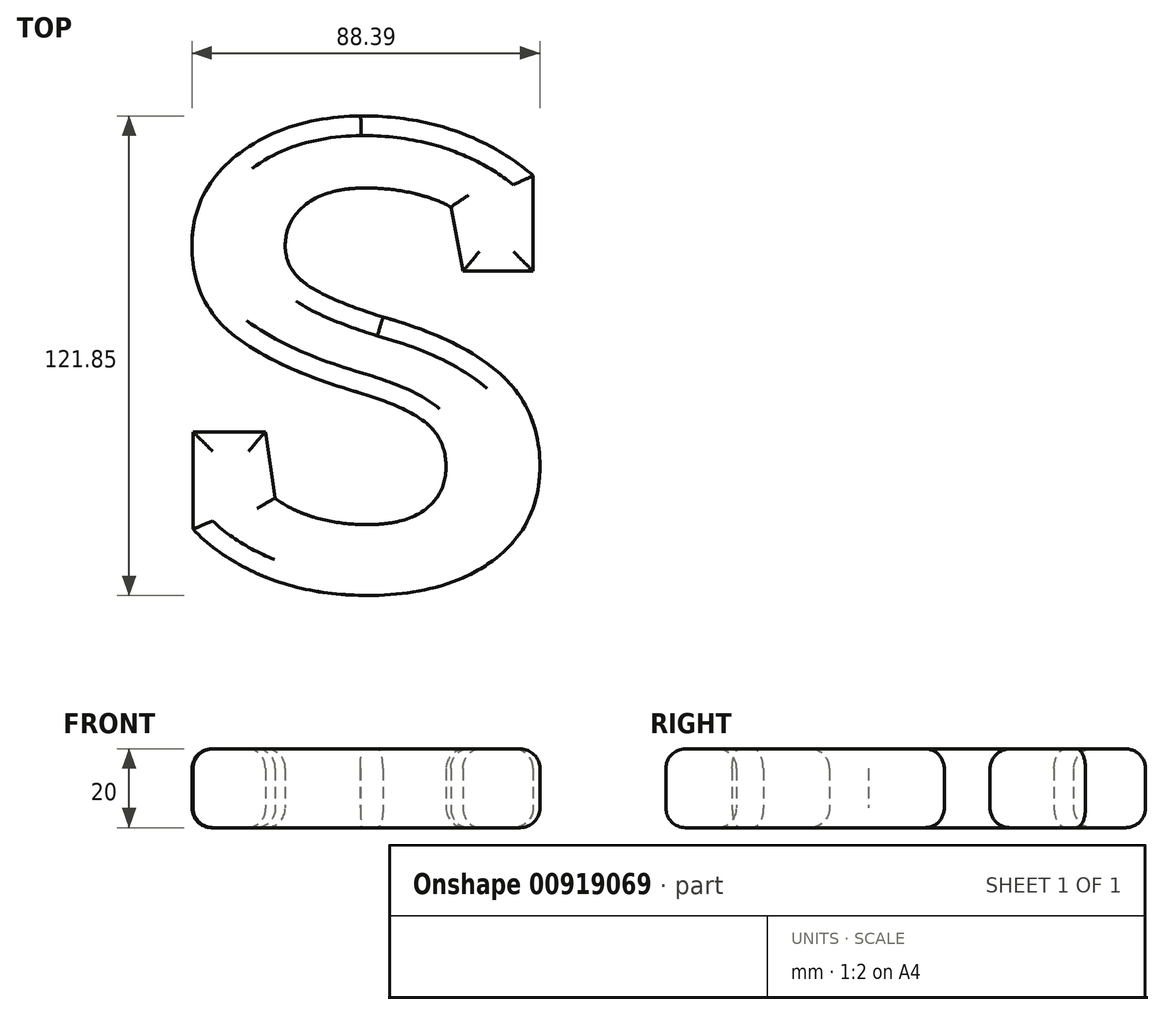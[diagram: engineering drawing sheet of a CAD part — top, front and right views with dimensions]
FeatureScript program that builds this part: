
annotation { "Feature Type Name" : "Feature", "Feature Type Description" : "" }
export const myFeature = defineFeature(function(context is Context, id is Id, definition is map)
    precondition{}
    {
        {
            var Q0;
            Q0=qCreatedBy(makeId("Top.planeOp"),FACE);
            var sketch = newSketch(context, id + "F0", { "sketchPlane" : qUnion([Q0])});
            skText(sketch, "E0", { "text": "S", "fontName": "RobotoSlab-Bold.ttf"});
            const initialGuessF0  = {"E0": [-0.07053, -0.06391, 1, 0, 0.12]};
            skSetInitialGuess(sketch, initialGuessF0);
            skSolve(sketch);
        }
        {
            var Q0;
            Q0 = qSketchRegion(id + "F0", true);
            extrude(context, id + "F1", {"entities" : qUnion([Q0]), "depth" : 20 * mm, "offsetDistance" : 25 * mm});
        }
        {
            var Q0;
            Q0=makeQuery(id+"F1.opExtrude","CAP_FACE",FACE,{"disambiguationData":[OSD([sQuery(id+"F0.wireOp",EDGE,"E0.sketch_text.stroke-0"),sQuery(id+"F0.wireOp",EDGE,"E0.sketch_text.stroke-1"),sQuery(id+"F0.wireOp",EDGE,"E0.sketch_text.stroke-2"),sQuery(id+"F0.wireOp",EDGE,"E0.sketch_text.stroke-3"),sQuery(id+"F0.wireOp",EDGE,"E0.sketch_text.stroke-4"),sQuery(id+"F0.wireOp",EDGE,"E0.sketch_text.stroke-5"),sQuery(id+"F0.wireOp",EDGE,"E0.sketch_text.stroke-6"),sQuery(id+"F0.wireOp",EDGE,"E0.sketch_text.stroke-7"),sQuery(id+"F0.wireOp",EDGE,"E0.sketch_text.stroke-8"),sQuery(id+"F0.wireOp",EDGE,"E0.sketch_text.stroke-9"),sQuery(id+"F0.wireOp",EDGE,"E0.sketch_text.stroke-10"),sQuery(id+"F0.wireOp",EDGE,"E0.sketch_text.stroke-11"),sQuery(id+"F0.wireOp",EDGE,"E0.sketch_text.stroke-12"),sQuery(id+"F0.wireOp",EDGE,"E0.sketch_text.stroke-13"),sQuery(id+"F0.wireOp",EDGE,"E0.sketch_text.stroke-14"),sQuery(id+"F0.wireOp",EDGE,"E0.sketch_text.stroke-15"),sQuery(id+"F0.wireOp",EDGE,"E0.sketch_text.stroke-16"),sQuery(id+"F0.wireOp",EDGE,"E0.sketch_text.stroke-17"),sQuery(id+"F0.wireOp",EDGE,"E0.sketch_text.stroke-18"),sQuery(id+"F0.wireOp",EDGE,"E0.sketch_text.stroke-19"),sQuery(id+"F0.wireOp",EDGE,"E0.sketch_text.stroke-20"),sQuery(id+"F0.wireOp",EDGE,"E0.sketch_text.stroke-21"),sQuery(id+"F0.wireOp",EDGE,"E0.sketch_text.stroke-22"),sQuery(id+"F0.wireOp",EDGE,"E0.sketch_text.stroke-23"),sQuery(id+"F0.wireOp",EDGE,"E0.sketch_text.stroke-24"),sQuery(id+"F0.wireOp",EDGE,"E0.sketch_text.stroke-25"),sQuery(id+"F0.wireOp",EDGE,"E0.sketch_text.stroke-26"),sQuery(id+"F0.wireOp",EDGE,"E0.sketch_text.stroke-27"),sQuery(id+"F0.wireOp",EDGE,"E0.sketch_text.stroke-28"),sQuery(id+"F0.wireOp",EDGE,"E0.sketch_text.stroke-29")])],"isStart":true});
            var Q1;
            Q1=makeQuery(id+"F1.opExtrude","CAP_FACE",FACE,{"disambiguationData":[OSD([sQuery(id+"F0.wireOp",EDGE,"E0.sketch_text.stroke-0"),sQuery(id+"F0.wireOp",EDGE,"E0.sketch_text.stroke-1"),sQuery(id+"F0.wireOp",EDGE,"E0.sketch_text.stroke-2"),sQuery(id+"F0.wireOp",EDGE,"E0.sketch_text.stroke-3"),sQuery(id+"F0.wireOp",EDGE,"E0.sketch_text.stroke-4"),sQuery(id+"F0.wireOp",EDGE,"E0.sketch_text.stroke-5"),sQuery(id+"F0.wireOp",EDGE,"E0.sketch_text.stroke-6"),sQuery(id+"F0.wireOp",EDGE,"E0.sketch_text.stroke-7"),sQuery(id+"F0.wireOp",EDGE,"E0.sketch_text.stroke-8"),sQuery(id+"F0.wireOp",EDGE,"E0.sketch_text.stroke-9"),sQuery(id+"F0.wireOp",EDGE,"E0.sketch_text.stroke-10"),sQuery(id+"F0.wireOp",EDGE,"E0.sketch_text.stroke-11"),sQuery(id+"F0.wireOp",EDGE,"E0.sketch_text.stroke-12"),sQuery(id+"F0.wireOp",EDGE,"E0.sketch_text.stroke-13"),sQuery(id+"F0.wireOp",EDGE,"E0.sketch_text.stroke-14"),sQuery(id+"F0.wireOp",EDGE,"E0.sketch_text.stroke-15"),sQuery(id+"F0.wireOp",EDGE,"E0.sketch_text.stroke-16"),sQuery(id+"F0.wireOp",EDGE,"E0.sketch_text.stroke-17"),sQuery(id+"F0.wireOp",EDGE,"E0.sketch_text.stroke-18"),sQuery(id+"F0.wireOp",EDGE,"E0.sketch_text.stroke-19"),sQuery(id+"F0.wireOp",EDGE,"E0.sketch_text.stroke-20"),sQuery(id+"F0.wireOp",EDGE,"E0.sketch_text.stroke-21"),sQuery(id+"F0.wireOp",EDGE,"E0.sketch_text.stroke-22"),sQuery(id+"F0.wireOp",EDGE,"E0.sketch_text.stroke-23"),sQuery(id+"F0.wireOp",EDGE,"E0.sketch_text.stroke-24"),sQuery(id+"F0.wireOp",EDGE,"E0.sketch_text.stroke-25"),sQuery(id+"F0.wireOp",EDGE,"E0.sketch_text.stroke-26"),sQuery(id+"F0.wireOp",EDGE,"E0.sketch_text.stroke-27"),sQuery(id+"F0.wireOp",EDGE,"E0.sketch_text.stroke-28"),sQuery(id+"F0.wireOp",EDGE,"E0.sketch_text.stroke-29")])],"isStart":false});
            fillet(context, id + "F2", {"entities" : qUnion([Q0, Q1]), "radius" : 5 * mm, "tangentPropagation" : true, "allowEdgeOverflow" : false});
        }
    });
